# Revit family: Shades-Hunter_Douglas-RB500-Single_Heavy_Duty-Auto-Dual_7in_UM
name_source: partatom
category: Specialty Equipment
units: mm (PartAtom-declared; Revit-internal decimal feet)

## family parameters
Always vertical = Yes
Classification Number = 23.30.60.14
Cut with Voids When Loaded = No
Enable Cutting in Views = No
Maintain Annotation Orientation = No
Part Type = Normal
Room Calculation Point = No
Round Connector Dimension = Use Diameter
Shared = No
Work Plane-Based = No

## types (2) — shared parameters
Assembly Code = E2010300
CD_Bracket Depth = 0' - 5 7/8"
CD_Bracket Height = 0' - 7 15/32"
CD_Fabric Sizing Disclaimer = Designer to verify maximum fabric size with Manufacturer as the maximum fabric size is dependent on finished dimensions
CD_Finish = Fabric-Shade-Hunter_Douglas-5%-E_Screen-Charcoal_Cocoa
CD_Finish Frame = Metal-Aluminum-Hunter_Douglas-Anodized
CD_Finish Rail = Metal-Aluminum-Hunter_Douglas-Anodized
CD_Install Documentation = https://www.hunterdouglasarchitectural.com
CD_Microsite = https://microsite.caddetails.com
CD_Product Documentation Link = https://www.hunterdouglasarchitectural.com
CD_Product Name = RB 500 Roller Shade System
CD_Product Page URL = https://www.hunterdouglasarchitectural.com
CD_Screen Offset From Face = 0' - 0 27/32"
CD_Warranty = https://assets.hunterdouglasarchitectural.com
Default Elevation = 0' - 0"
Description = Heavy Duty Automatic Roller Shade
Manufacturer = Hunter Douglas Architectural
Model = Heavy Duty Automated Dual 7in UM
URL = https://www.hunterdouglasarchitectural.com

## per-type parameters (varying)
| type | CD_Side Mount | CD_Top Mount |
| Top Mounted | No | Yes |
| Side Mounted | Yes | No |

note: column(s) folded — value = type name in every type: Type Comments

## geometry (parser evidence)
native form markers: Sweep x3
no freeform markers — native parametric forms only
